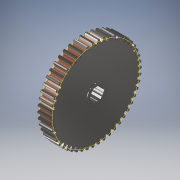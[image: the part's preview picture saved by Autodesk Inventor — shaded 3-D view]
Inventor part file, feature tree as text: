
AUTODESK INVENTOR PART (.ipt)
format: ipt  version: 2018 (Build 220112000, 112)  size: 443,392 bytes
history: native  units: in
note: dims shown in document units (in); Inventor stores cm internally (conversion verified against a paired STEP export)
features: other x3, sketch x1
ambient origin geometry x8: Origin, YZ Plane, XZ Plane, XY Plane, X Axis, Y Axis, Z Axis, Center Point
bodies: Solid1 (feature_tree)
feature tree (4):
  sketch  "Sketch1"  dims[d0=2.5in d1=1.0in d2=0.0in]
  other  "Srf1"
  other  "Cut-Extrude2"
  other  "PITCH CIRCLE"
